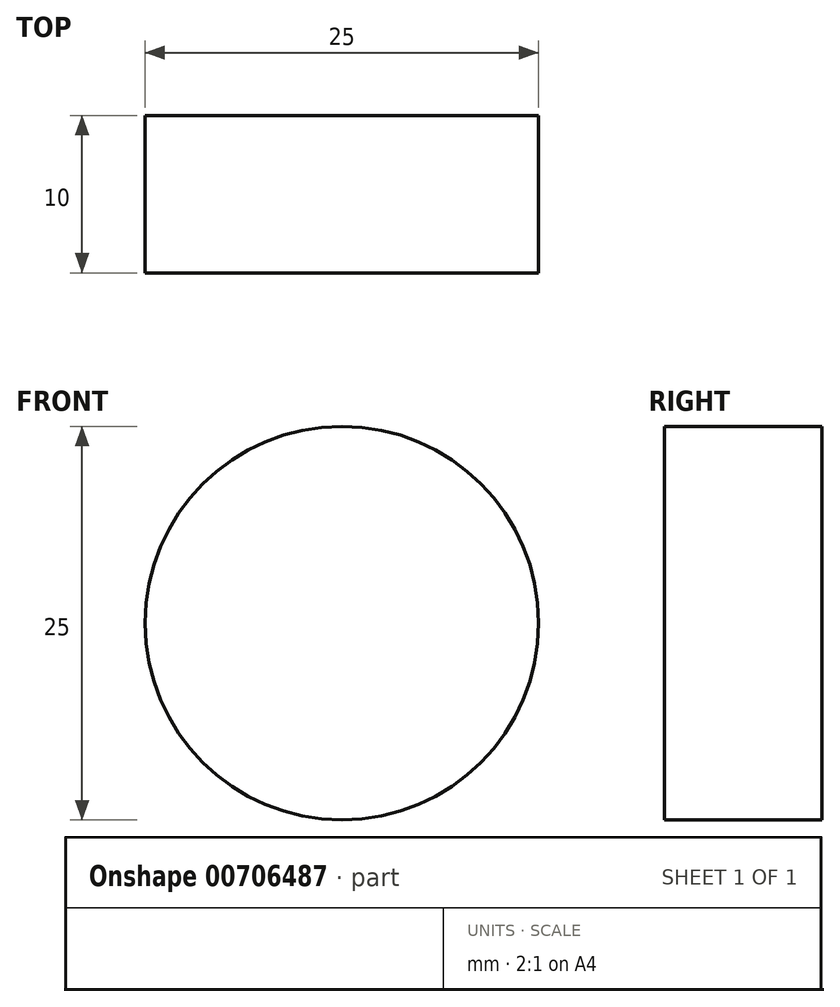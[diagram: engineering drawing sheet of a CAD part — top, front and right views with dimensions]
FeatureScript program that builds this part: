
annotation { "Feature Type Name" : "Feature", "Feature Type Description" : "" }
export const myFeature = defineFeature(function(context is Context, id is Id, definition is map)
    precondition{}
    {
        {
            var Q0;
            Q0=qCreatedBy(makeId("Front.planeOp"),FACE);
            var sketch = newSketch(context, id + "F0", { "sketchPlane" : qUnion([Q0])});
            skCircle(sketch, "E0", {"center": v(-0.05, -0.07) * mm, "radius": 12.5 * mm});
            skSolve(sketch);
        }
        {
            var Q0;
            Q0 = qSketchRegion(id + "F0", true);
            extrude(context, id + "F1", {"entities" : qUnion([Q0]), "depth" : 10 * mm, "offsetDistance" : 25 * mm});
        }
    });
